# Revit family: PRD_FrankeWS_PprTwlDpnsrs_EXOSPaperTowelDispenser_EXOS600X,600B,600W
name_source: partatom
category: Furniture
revit_build: Autodesk Revit 2018 (Build: 20190510_1515(x64)
units: mm (PartAtom-declared; Revit-internal decimal feet)

## family parameters
Cut with Voids When Loaded = No
Host = Face
OmniClass Number = 23.40.20.21
OmniClass Title = Toilet and Bath Specialties
Room Calculation Point = No
Shared = No

## types (3) — shared parameters
AssetType = Fixed
Category = Pr_40_70_22_62, Paper towel dispensers
Color = Stainless steel
Default Elevation = 1200 mm
DispenserMaterial = PRD_AR_StainlessSteel_SatinFinished
DurationUnit = year
FillingQuantity = 400 towels
Finish = Satin finished
Form = Wall mounted
IfcExportAs = IfcFurnitureType
IfcExportType = NOTDEFINED
IntegralAccessories = includes mounting materials
Lock = key-lock
MainColor = Stainless steel
Manufacturer = KWC Group AG
ManufacturerName = KWC Group AG
ManufacturerURL = www.kwc.com
Material = Stainless steel
MaterialCode = Stainless steel 1.4301
MaterialThickness = 1.20 mm
NBSDescription = Paper towel dispensers
NBSReference = 45-35-72/344
NominalDepth = 120 mm  [stored 0.393701 ft]
NominalWidth = 300 mm
Operation = Manual
ProductInformation = https://pim.kwc.com
Size = 300 x 325 x 120 mm
Style = Paper towel dispenser
SurfaceTreatment = InoxPlus
TypeOfConsumable = Paper towel
TypeOfFixing = Screw
TypeOfMounting = Wall mounting
TypeOfOperation = Manual operation
URL = www.kwc.com
Uniclass2015Code = Pr_40_70_22_62
Uniclass2015Title = Paper towel dispensers
Uniclass2015Version = Products v1.10
Version = 1
WarrantyDurationUnit = year

## per-type parameters (varying)
| type | BIMObjectName | Description | Features | GrossWeight | ModelNumber | Name | NetWeight | NominalHeight | PanelMaterial |
| EXOS600B | PRD_AR_PaperTowelDispensers_EXOSPaperTowelDispenser_EXOS600B | Paper towel dispenser for wall mounting, stainless steel with satin finish, black safety glass front panel, casing with InoxPlus surface refinement for the reduction of finger marks and better cleaning characteristics (easy to clean), material thickness 1.2 mm, inspection window on side, capacity 300 - 400 pieces of Z-folded paper, includes mounting materials.Dimensions: 300 x 326 x 120 mm (W x H x D) | for wall mounting. Dimensions: 300 x 325 x 120 mm (W x H x D) | 5.10 kg | 2030022934 | EXOS paper towel dispenser EXOS600B | 4.67 kg | 326 mm  [stored 1.06955 ft] | PRD_AR_Glass_Black |
| EXOS600W | PRD_AR_PaperTowelDispensers_EXOSPaperTowelDispenser_EXOS600W | Paper towel dispenser for wall mounting, stainless steel with satin finish, white safety glass front panel, casing with InoxPlus surface refinement for the reduction of finger marks and better cleaning characteristics (easy to clean), material thickness 1.2 mm, inspection window on side, capacity 300 - 400 pieces of Z-folded paper, includes mounting materials. | For wall mounting. Dimensions: 300 x 325 x 120 mm (W x H x D) | 5.06 kg | 2030025229 | EXOS Paper towel dispenser EXOS600W | 4.64 kg | 325 mm  [stored 1.06627 ft] | PRD_AR_Glass_White |
| EXOS600X | PRD_AR_PaperTowelDispensers_EXOSPaperTowelDispenser_EXOS600X | Paper towel dispenser for wall mounting, stainless steel with satin finish, front and casing with InoxPlus surface refinement for the reduction of finger marks and better cleaning characteristics (easy to clean), material thickness 1.2 mm, inspection window on side, capacity 300 - 400 pieces of Z-folded paper, includes mounting materials. | For wall mounting. Dimensions: 300 x 325 x 120 mm (W x H x D) | 4.36 kg | 2030022933 | EXOS Paper towel dispenser EXOS600X | 3.98 kg | 325 mm  [stored 1.06627 ft] | PRD_AR_StainlessSteel_SatinFinished |

note: column(s) folded — value = type name in every type: Model, ModelReference

note: [stored X ft] marks values corroborated as IEEE doubles in the binary element streams (Revit-internal decimal feet)

## geometry (parser evidence)
native form markers: Sweep x2
no freeform markers — native parametric forms only
